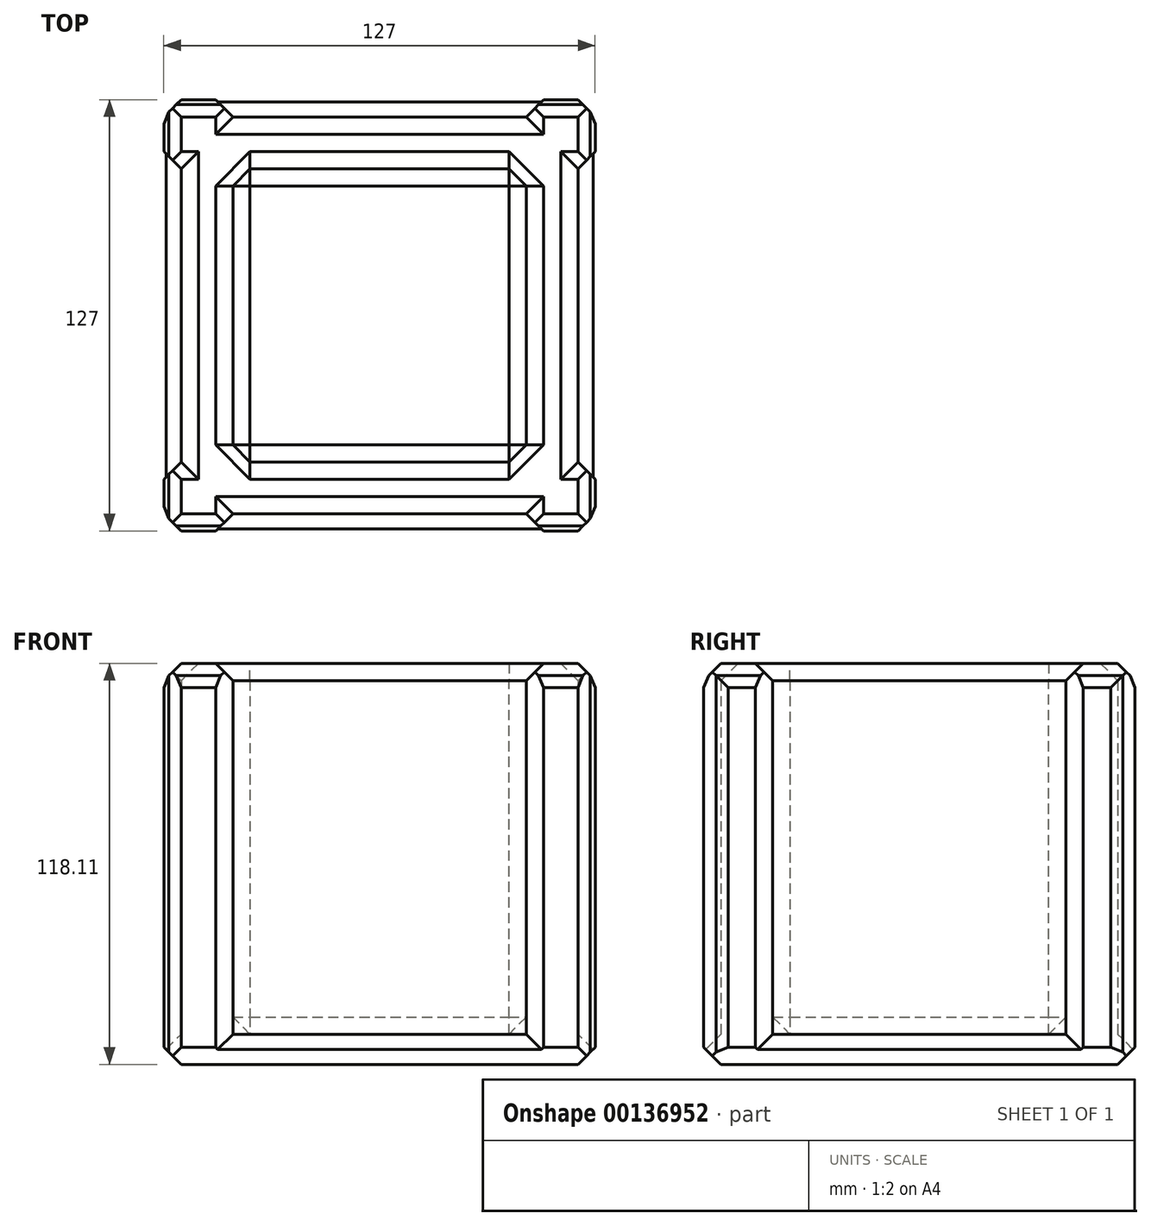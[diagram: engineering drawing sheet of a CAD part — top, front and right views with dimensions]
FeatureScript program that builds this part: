
annotation { "Feature Type Name" : "Feature", "Feature Type Description" : "" }
export const myFeature = defineFeature(function(context is Context, id is Id, definition is map)
    precondition{}
    {
        {
            var Q0;
            Q0=qCreatedBy(makeId("Top.planeOp"),FACE);
            var sketch = newSketch(context, id + "F0", { "sketchPlane" : qUnion([Q0])});
            skLineSegment(sketch, "E0.bottom", {"start": v(-59.79, 56.04) * mm, "end": v(67.21, 56.04) * mm});
            skLineSegment(sketch, "E0.top", {"start": v(-59.79, -70.96) * mm, "end": v(67.21, -70.96) * mm});
            skLineSegment(sketch, "E0.left", {"start": v(-59.79, 56.04) * mm, "end": v(-59.79, -70.96) * mm});
            skLineSegment(sketch, "E0.right", {"start": v(67.21, 56.04) * mm, "end": v(67.21, -70.96) * mm});
            skSolve(sketch);
        }
        {
            var Q0;
            Q0=makeQuery(id+"F0.imprint","IMPRINT",FACE,{"disambiguationData":[TD([[makeQuery(id+"F0.imprint","IMPRINT",EDGE,{"derivedFrom":sQuery(id+"F0.wireOp",EDGE,"E0.bottom")}),-1.0]])]});
            extrude(context, id + "F1", {"entities" : qUnion([Q0]), "depth" : 8.9 * mm});
        }
        {
            var Q0;
            Q0=makeQuery(id+"F1.opExtrude","CAP_FACE",FACE,{"disambiguationData":[OSD([sQuery(id+"F0.wireOp",EDGE,"E0.bottom"),sQuery(id+"F0.wireOp",EDGE,"E0.top"),sQuery(id+"F0.wireOp",EDGE,"E0.left"),sQuery(id+"F0.wireOp",EDGE,"E0.right")])],"isStart":false});
            var sketch = newSketch(context, id + "F2", { "sketchPlane" : qUnion([Q0])});
            skLineSegment(sketch, "E1.bottom", {"start": v(-59.79, -70.96) * mm, "end": v(-39.47, -70.96) * mm});
            skLineSegment(sketch, "E1.top", {"start": v(-59.79, -50.64) * mm, "end": v(-39.47, -50.64) * mm});
            skLineSegment(sketch, "E1.left", {"start": v(-59.79, -70.96) * mm, "end": v(-59.79, -50.64) * mm});
            skLineSegment(sketch, "E1.right", {"start": v(-39.47, -70.96) * mm, "end": v(-39.47, -50.64) * mm});
            skLineSegment(sketch, "E2.bottom", {"start": v(-59.79, 56.04) * mm, "end": v(-39.47, 56.04) * mm});
            skLineSegment(sketch, "E2.top", {"start": v(-59.79, 35.72) * mm, "end": v(-39.47, 35.72) * mm});
            skLineSegment(sketch, "E2.left", {"start": v(-59.79, 56.04) * mm, "end": v(-59.79, 35.72) * mm});
            skLineSegment(sketch, "E2.right", {"start": v(-39.47, 56.04) * mm, "end": v(-39.47, 35.72) * mm});
            skLineSegment(sketch, "E3.bottom", {"start": v(67.21, 56.04) * mm, "end": v(46.9, 56.04) * mm});
            skLineSegment(sketch, "E3.top", {"start": v(67.21, 35.72) * mm, "end": v(46.9, 35.72) * mm});
            skLineSegment(sketch, "E3.left", {"start": v(67.21, 56.04) * mm, "end": v(67.21, 35.72) * mm});
            skLineSegment(sketch, "E3.right", {"start": v(46.9, 56.04) * mm, "end": v(46.9, 35.72) * mm});
            skLineSegment(sketch, "E4.bottom", {"start": v(67.21, -70.96) * mm, "end": v(46.9, -70.96) * mm});
            skLineSegment(sketch, "E4.top", {"start": v(67.21, -50.64) * mm, "end": v(46.9, -50.64) * mm});
            skLineSegment(sketch, "E4.left", {"start": v(67.21, -70.96) * mm, "end": v(67.21, -50.64) * mm});
            skLineSegment(sketch, "E4.right", {"start": v(46.9, -70.96) * mm, "end": v(46.9, -50.64) * mm});
            skLineSegment(sketch, "E5", {"start": v(-39.47, 45.88) * mm, "end": v(46.9, 45.88) * mm});
            skLineSegment(sketch, "E6", {"start": v(57.05, 35.72) * mm, "end": v(57.05, -50.64) * mm});
            skLineSegment(sketch, "E7", {"start": v(46.9, -60.8) * mm, "end": v(-39.47, -60.8) * mm});
            skLineSegment(sketch, "E8", {"start": v(-49.63, -50.64) * mm, "end": v(-49.63, 35.72) * mm});
            skLineSegment(sketch, "E9", {"start": v(-39.47, 35.72) * mm, "end": v(-39.47, -50.64) * mm});
            skLineSegment(sketch, "E10", {"start": v(-39.47, -50.64) * mm, "end": v(46.9, -50.64) * mm});
            skLineSegment(sketch, "E11", {"start": v(46.9, -50.64) * mm, "end": v(46.9, 35.72) * mm});
            skLineSegment(sketch, "E12", {"start": v(46.9, 35.72) * mm, "end": v(-39.47, 35.72) * mm});
            skSolve(sketch);
        }
        {
            var Q0;
            {var subQ5=sQuery(id+"F2.wireOp",EDGE,"E2.bottom");Q0=makeQuery(id+"F2.imprint","IMPRINT",FACE,{"disambiguationData":[TD([[makeQuery(id+"F2.imprint","IMPRINT",EDGE,{"derivedFrom":subQ5}),-1.0]])]});}
            var Q1;
            {var subQ2=sQuery(id+"F2.wireOp",EDGE,"E5");Q1=makeQuery(id+"F2.imprint","IMPRINT",FACE,{"disambiguationData":[TD([[makeQuery(id+"F2.imprint","IMPRINT",EDGE,{"derivedFrom":subQ2}),-1.0]])]});}
            var Q2;
            {var subQ6=sQuery(id+"F2.wireOp",EDGE,"E3.bottom");Q2=makeQuery(id+"F2.imprint","IMPRINT",FACE,{"disambiguationData":[TD([[makeQuery(id+"F2.imprint","IMPRINT",EDGE,{"derivedFrom":subQ6}),-1.0]])]});}
            var Q3;
            {var subQ2=sQuery(id+"F2.wireOp",EDGE,"E6");Q3=makeQuery(id+"F2.imprint","IMPRINT",FACE,{"disambiguationData":[TD([[makeQuery(id+"F2.imprint","IMPRINT",EDGE,{"derivedFrom":subQ2}),-1.0]])]});}
            var Q4;
            {var subQ2=sQuery(id+"F2.wireOp",EDGE,"E8");Q4=makeQuery(id+"F2.imprint","IMPRINT",FACE,{"disambiguationData":[TD([[makeQuery(id+"F2.imprint","IMPRINT",EDGE,{"derivedFrom":subQ2}),-1.0]])]});}
            var Q5;
            {var subQ5=sQuery(id+"F2.wireOp",EDGE,"E1.bottom");Q5=makeQuery(id+"F2.imprint","IMPRINT",FACE,{"disambiguationData":[TD([[makeQuery(id+"F2.imprint","IMPRINT",EDGE,{"derivedFrom":subQ5}),1.0]])]});}
            var Q6;
            {var subQ5=sQuery(id+"F2.wireOp",EDGE,"E4.bottom");Q6=makeQuery(id+"F2.imprint","IMPRINT",FACE,{"disambiguationData":[TD([[makeQuery(id+"F2.imprint","IMPRINT",EDGE,{"derivedFrom":subQ5}),1.0]])]});}
            var Q7;
            {var subQ2=sQuery(id+"F2.wireOp",EDGE,"E7");Q7=makeQuery(id+"F2.imprint","IMPRINT",FACE,{"disambiguationData":[TD([[makeQuery(id+"F2.imprint","IMPRINT",EDGE,{"derivedFrom":subQ2}),-1.0]])]});}
            extrude(context, id + "F3", {"entities" : qUnion([Q0, Q1, Q2, Q3, Q4, Q5, Q6, Q7]), "operationType" : NewBodyOperationType.ADD, "depth" : 101.6 * mm});
        }
        {
            var Q0;
            Q0=makeQuery(id+"F3.opExtrude","CAP_FACE",FACE,{"disambiguationData":[OSD([sQuery(id+"F2.wireOp",EDGE,"E1.bottom"),sQuery(id+"F2.wireOp",EDGE,"E1.top"),sQuery(id+"F2.wireOp",EDGE,"E1.left"),sQuery(id+"F2.wireOp",EDGE,"E1.right"),sQuery(id+"F2.wireOp",EDGE,"E2.bottom"),sQuery(id+"F2.wireOp",EDGE,"E2.top"),sQuery(id+"F2.wireOp",EDGE,"E2.left"),sQuery(id+"F2.wireOp",EDGE,"E2.right"),sQuery(id+"F2.wireOp",EDGE,"E3.bottom"),sQuery(id+"F2.wireOp",EDGE,"E3.top"),sQuery(id+"F2.wireOp",EDGE,"E3.left"),sQuery(id+"F2.wireOp",EDGE,"E3.right"),sQuery(id+"F2.wireOp",EDGE,"E4.bottom"),sQuery(id+"F2.wireOp",EDGE,"E4.top"),sQuery(id+"F2.wireOp",EDGE,"E4.left"),sQuery(id+"F2.wireOp",EDGE,"E4.right"),sQuery(id+"F2.wireOp",EDGE,"E5"),sQuery(id+"F2.wireOp",EDGE,"E6"),sQuery(id+"F2.wireOp",EDGE,"E7"),sQuery(id+"F2.wireOp",EDGE,"E8"),sQuery(id+"F2.wireOp",EDGE,"E9"),sQuery(id+"F2.wireOp",EDGE,"E10"),sQuery(id+"F2.wireOp",EDGE,"E11"),sQuery(id+"F2.wireOp",EDGE,"E12")])],"isStart":false});
            var sketch = newSketch(context, id + "F4", { "sketchPlane" : qUnion([Q0])});
            skLineSegment(sketch, "E13.0", {"start": v(52.05, 50.89) * mm, "end": v(52.05, 40.87) * mm});
            skLineSegment(sketch, "E13.1", {"start": v(62.06, 50.89) * mm, "end": v(52.05, 50.89) * mm});
            skLineSegment(sketch, "E13.2", {"start": v(62.06, -55.8) * mm, "end": v(52.05, -55.8) * mm});
            skLineSegment(sketch, "E13.3", {"start": v(62.06, -65.81) * mm, "end": v(62.06, -55.8) * mm});
            skLineSegment(sketch, "E13.4", {"start": v(-44.62, -65.81) * mm, "end": v(-44.62, -55.8) * mm});
            skLineSegment(sketch, "E13.5", {"start": v(62.06, 40.87) * mm, "end": v(62.06, 50.89) * mm});
            skLineSegment(sketch, "E13.6", {"start": v(-54.63, -65.81) * mm, "end": v(-44.62, -65.81) * mm});
            skLineSegment(sketch, "E13.7", {"start": v(-54.63, 50.89) * mm, "end": v(-54.63, 40.87) * mm});
            skLineSegment(sketch, "E13.8", {"start": v(-54.63, 40.87) * mm, "end": v(-44.62, 40.87) * mm});
            skLineSegment(sketch, "E13.9", {"start": v(52.05, -65.81) * mm, "end": v(62.06, -65.81) * mm});
            skLineSegment(sketch, "E13.10", {"start": v(51.9, -55.65) * mm, "end": v(51.9, 40.73) * mm});
            skLineSegment(sketch, "E13.11", {"start": v(-44.47, 40.73) * mm, "end": v(-44.47, -55.65) * mm});
            skLineSegment(sketch, "E13.12", {"start": v(51.9, 40.73) * mm, "end": v(-44.47, 40.73) * mm});
            skLineSegment(sketch, "E13.13", {"start": v(52.05, -55.8) * mm, "end": v(52.05, -65.81) * mm});
            skLineSegment(sketch, "E13.14", {"start": v(-44.47, -55.65) * mm, "end": v(51.9, -55.65) * mm});
            skLineSegment(sketch, "E13.15", {"start": v(-44.62, 40.87) * mm, "end": v(-44.62, 50.89) * mm});
            skLineSegment(sketch, "E13.16", {"start": v(-44.62, -55.8) * mm, "end": v(-54.63, -55.8) * mm});
            skLineSegment(sketch, "E13.17", {"start": v(52.05, 40.87) * mm, "end": v(62.06, 40.87) * mm});
            skLineSegment(sketch, "E13.18", {"start": v(-44.62, 50.89) * mm, "end": v(-54.63, 50.89) * mm});
            skLineSegment(sketch, "E13.19", {"start": v(-54.63, -55.8) * mm, "end": v(-54.63, -65.81) * mm});
            skSolve(sketch);
        }
        {
            var Q0;
            Q0=makeQuery(id+"F4.imprint","IMPRINT",FACE,{"disambiguationData":[TD([[makeQuery(id+"F4.imprint","IMPRINT",EDGE,{"derivedFrom":sQuery(id+"F4.wireOp",EDGE,"E13.10")}),1.0]])]});
            var Q1;
            Q1=makeQuery(id+"F4.imprint","IMPRINT",FACE,{"disambiguationData":[TD([[makeQuery(id+"F4.imprint","IMPRINT",EDGE,{"derivedFrom":sQuery(id+"F4.wireOp",EDGE,"E13.7")}),1.0]])]});
            var Q2;
            Q2=makeQuery(id+"F4.imprint","IMPRINT",FACE,{"disambiguationData":[TD([[makeQuery(id+"F4.imprint","IMPRINT",EDGE,{"derivedFrom":sQuery(id+"F4.wireOp",EDGE,"E13.0")}),1.0]])]});
            var Q3;
            Q3=makeQuery(id+"F4.imprint","IMPRINT",FACE,{"disambiguationData":[TD([[makeQuery(id+"F4.imprint","IMPRINT",EDGE,{"derivedFrom":sQuery(id+"F4.wireOp",EDGE,"E13.4")}),1.0]])]});
            var Q4;
            Q4=makeQuery(id+"F4.imprint","IMPRINT",FACE,{"disambiguationData":[TD([[makeQuery(id+"F4.imprint","IMPRINT",EDGE,{"derivedFrom":sQuery(id+"F4.wireOp",EDGE,"E13.2")}),1.0]])]});
            var Q5;
            Q5=makeQuery(id+"F4.imprint","IMPRINT",FACE,{"disambiguationData":[TD([[makeQuery(id+"F4.imprint","IMPRINT",EDGE,{"derivedFrom":sQuery(id+"F4.wireOp",EDGE,"E13.0")}),-1.0]])]});
            extrude(context, id + "F5", {"entities" : qUnion([Q0, Q1, Q2, Q3, Q4, Q5]), "operationType" : NewBodyOperationType.ADD, "depth" : 7.62 * mm});
        }
        {
            var Q0;
            {var subQ0=sQuery(id+"F0.wireOp",EDGE,"E0.bottom");Q0=makeQuery(id+"F3.boolean.opBoolean","SPLIT",FACE,{"disambiguationData":[TD([makeQuery(id+"F1.opExtrude","SWEPT_FACE",FACE,{"disambiguationData":[OSD([subQ0])]})])],"derivedFrom":makeQuery(id+"F1.opExtrude","CAP_FACE",FACE,{"disambiguationData":[OSD([subQ0,sQuery(id+"F0.wireOp",EDGE,"E0.top"),sQuery(id+"F0.wireOp",EDGE,"E0.left"),sQuery(id+"F0.wireOp",EDGE,"E0.right")])],"isStart":false})});}
            var sketch = newSketch(context, id + "F6", { "sketchPlane" : qUnion([Q0])});
            skLineSegment(sketch, "E14", {"start": v(-39.47, 50.96) * mm, "end": v(46.9, 50.96) * mm});
            skSolve(sketch);
        }
        {
            var Q0;
            {var subQ0=sQuery(id+"F0.wireOp",EDGE,"E0.right");Q0=makeQuery(id+"F3.boolean.opBoolean","SPLIT",FACE,{"disambiguationData":[TD([makeQuery(id+"F1.opExtrude","SWEPT_FACE",FACE,{"disambiguationData":[OSD([subQ0])]})])],"derivedFrom":makeQuery(id+"F1.opExtrude","CAP_FACE",FACE,{"disambiguationData":[OSD([sQuery(id+"F0.wireOp",EDGE,"E0.bottom"),sQuery(id+"F0.wireOp",EDGE,"E0.top"),sQuery(id+"F0.wireOp",EDGE,"E0.left"),subQ0])],"isStart":false})});}
            var sketch = newSketch(context, id + "F7", { "sketchPlane" : qUnion([Q0])});
            skLineSegment(sketch, "E15", {"start": v(62.13, -50.64) * mm, "end": v(62.13, 35.72) * mm});
            skSolve(sketch);
        }
        {
            var Q0;
            {var subQ0=sQuery(id+"F0.wireOp",EDGE,"E0.top");Q0=makeQuery(id+"F3.boolean.opBoolean","SPLIT",FACE,{"disambiguationData":[TD([makeQuery(id+"F1.opExtrude","SWEPT_FACE",FACE,{"disambiguationData":[OSD([subQ0])]})])],"derivedFrom":makeQuery(id+"F1.opExtrude","CAP_FACE",FACE,{"disambiguationData":[OSD([sQuery(id+"F0.wireOp",EDGE,"E0.bottom"),subQ0,sQuery(id+"F0.wireOp",EDGE,"E0.left"),sQuery(id+"F0.wireOp",EDGE,"E0.right")])],"isStart":false})});}
            var sketch = newSketch(context, id + "F8", { "sketchPlane" : qUnion([Q0])});
            skLineSegment(sketch, "E16", {"start": v(46.9, -65.88) * mm, "end": v(-39.47, -65.88) * mm});
            skSolve(sketch);
        }
        {
            var Q0;
            {var subQ0=sQuery(id+"F0.wireOp",EDGE,"E0.left");Q0=makeQuery(id+"F3.boolean.opBoolean","SPLIT",FACE,{"disambiguationData":[TD([makeQuery(id+"F1.opExtrude","SWEPT_FACE",FACE,{"disambiguationData":[OSD([subQ0])]})])],"derivedFrom":makeQuery(id+"F1.opExtrude","CAP_FACE",FACE,{"disambiguationData":[OSD([sQuery(id+"F0.wireOp",EDGE,"E0.bottom"),sQuery(id+"F0.wireOp",EDGE,"E0.top"),subQ0,sQuery(id+"F0.wireOp",EDGE,"E0.right")])],"isStart":false})});}
            var sketch = newSketch(context, id + "F9", { "sketchPlane" : qUnion([Q0])});
            skLineSegment(sketch, "E17", {"start": v(-54.7, -50.64) * mm, "end": v(-54.7, 35.72) * mm});
            skSolve(sketch);
        }
        {
            var Q0;
            {var subQ0=sQuery(id+"F6.wireOp",EDGE,"E14");Q0=makeQuery(id+"F6.imprint","IMPRINT",FACE,{"disambiguationData":[TD([[makeQuery(id+"F6.imprint","IMPRINT",EDGE,{"derivedFrom":subQ0}),-1.0]])]});}
            var Q1;
            {var subQ0=sQuery(id+"F9.wireOp",EDGE,"E17");Q1=makeQuery(id+"F9.imprint","IMPRINT",FACE,{"disambiguationData":[TD([[makeQuery(id+"F9.imprint","IMPRINT",EDGE,{"derivedFrom":subQ0}),-1.0]])]});}
            var Q2;
            {var subQ0=sQuery(id+"F7.wireOp",EDGE,"E15");Q2=makeQuery(id+"F7.imprint","IMPRINT",FACE,{"disambiguationData":[TD([[makeQuery(id+"F7.imprint","IMPRINT",EDGE,{"derivedFrom":subQ0}),1.0]])]});}
            var Q3;
            {var subQ0=sQuery(id+"F8.wireOp",EDGE,"E16");Q3=makeQuery(id+"F8.imprint","IMPRINT",FACE,{"disambiguationData":[TD([[makeQuery(id+"F8.imprint","IMPRINT",EDGE,{"derivedFrom":subQ0}),-1.0]])]});}
            extrude(context, id + "F10", {"entities" : qUnion([Q0, Q1, Q2, Q3]), "operationType" : NewBodyOperationType.ADD, "depth" : 109.22 * mm});
        }
        {
            var Q0;
            {var subQ0=sQuery(id+"F2.wireOp",EDGE,"E8");var subQ1=sQuery(id+"F2.wireOp",EDGE,"E2.top");var subQ2=sQuery(id+"F2.wireOp",EDGE,"E1.top");var subQ3=sQuery(id+"F2.wireOp",EDGE,"E7");var subQ4=sQuery(id+"F2.wireOp",EDGE,"E4.right");var subQ5=sQuery(id+"F2.wireOp",EDGE,"E1.right");var subQ6=sQuery(id+"F2.wireOp",EDGE,"E6");var subQ7=sQuery(id+"F2.wireOp",EDGE,"E4.top");var subQ8=sQuery(id+"F2.wireOp",EDGE,"E3.top");var subQ9=sQuery(id+"F2.wireOp",EDGE,"E5");var subQ10=sQuery(id+"F2.wireOp",EDGE,"E3.right");var subQ11=sQuery(id+"F2.wireOp",EDGE,"E2.right");Q0=makeQuery(id+"F10.boolean.opBoolean","MERGE",FACE,{"derivedFrom":[makeQuery(id+"F5.opExtrude","CAP_FACE",FACE,{"disambiguationData":[OSD([sQuery(id+"F2.wireOp",EDGE,"E1.bottom"),subQ2,sQuery(id+"F2.wireOp",EDGE,"E1.left"),subQ5,sQuery(id+"F2.wireOp",EDGE,"E2.bottom"),subQ1,sQuery(id+"F2.wireOp",EDGE,"E2.left"),subQ11,sQuery(id+"F2.wireOp",EDGE,"E3.bottom"),subQ8,sQuery(id+"F2.wireOp",EDGE,"E3.left"),subQ10,sQuery(id+"F2.wireOp",EDGE,"E4.bottom"),subQ7,sQuery(id+"F2.wireOp",EDGE,"E4.left"),subQ4,subQ9,subQ6,subQ3,subQ0,sQuery(id+"F2.wireOp",EDGE,"E9"),sQuery(id+"F2.wireOp",EDGE,"E10"),sQuery(id+"F2.wireOp",EDGE,"E11"),sQuery(id+"F2.wireOp",EDGE,"E12")])],"isStart":false}),makeQuery(id+"F10.opExtrude","CAP_FACE",FACE,{"disambiguationData":[OSD([subQ11,subQ10,subQ9,sQuery(id+"F6.wireOp",EDGE,"E14")])],"isStart":false}),makeQuery(id+"F10.opExtrude","CAP_FACE",FACE,{"disambiguationData":[OSD([subQ8,subQ7,subQ6,sQuery(id+"F7.wireOp",EDGE,"E15")])],"isStart":false}),makeQuery(id+"F10.opExtrude","CAP_FACE",FACE,{"disambiguationData":[OSD([subQ5,subQ4,subQ3,sQuery(id+"F8.wireOp",EDGE,"E16")])],"isStart":false}),makeQuery(id+"F10.opExtrude","CAP_FACE",FACE,{"disambiguationData":[OSD([subQ2,subQ1,subQ0,sQuery(id+"F9.wireOp",EDGE,"E17")])],"isStart":false})]});}
            var Q1;
            {var subQ0=sQuery(id+"F2.wireOp",EDGE,"E9");Q1=makeQuery(id+"F5.boolean.opBoolean","MERGE",FACE,{"derivedFrom":[makeQuery(id+"F3.opExtrude","SWEPT_FACE",FACE,{"disambiguationData":[OSD([subQ0])]}),makeQuery(id+"F5.opExtrude","SWEPT_FACE",FACE,{"disambiguationData":[OSD([subQ0])]})]});}
            var Q2;
            {var subQ0=sQuery(id+"F2.wireOp",EDGE,"E12");Q2=makeQuery(id+"F5.boolean.opBoolean","MERGE",FACE,{"derivedFrom":[makeQuery(id+"F3.opExtrude","SWEPT_FACE",FACE,{"disambiguationData":[OSD([subQ0])]}),makeQuery(id+"F5.opExtrude","SWEPT_FACE",FACE,{"disambiguationData":[OSD([subQ0])]})]});}
            var Q3;
            {var subQ0=sQuery(id+"F2.wireOp",EDGE,"E11");Q3=makeQuery(id+"F5.boolean.opBoolean","MERGE",FACE,{"derivedFrom":[makeQuery(id+"F3.opExtrude","SWEPT_FACE",FACE,{"disambiguationData":[OSD([subQ0])]}),makeQuery(id+"F5.opExtrude","SWEPT_FACE",FACE,{"disambiguationData":[OSD([subQ0])]})]});}
            var Q4;
            {var subQ0=sQuery(id+"F2.wireOp",EDGE,"E10");Q4=makeQuery(id+"F5.boolean.opBoolean","MERGE",FACE,{"derivedFrom":[makeQuery(id+"F3.opExtrude","SWEPT_FACE",FACE,{"disambiguationData":[OSD([subQ0])]}),makeQuery(id+"F5.opExtrude","SWEPT_FACE",FACE,{"disambiguationData":[OSD([subQ0])]})]});}
            chamfer(context, id + "F11", {"entities" : qUnion([Q0, Q1, Q2, Q3, Q4]), "width" : 5.08 * mm, "tangentPropagation" : true});
        }
        {
            var Q0;
            {var subQ0=sQuery(id+"F2.wireOp",EDGE,"E3.bottom");var subQ1=sQuery(id+"F2.wireOp",EDGE,"E2.bottom");Q0=makeQuery(id+"F5.boolean.opBoolean","MERGE",FACE,{"derivedFrom":[makeQuery(id+"F3.boolean.opBoolean","MERGE",FACE,{"derivedFrom":[makeQuery(id+"F1.opExtrude","SWEPT_FACE",FACE,{"disambiguationData":[OSD([sQuery(id+"F0.wireOp",EDGE,"E0.bottom")])]}),makeQuery(id+"F3.opExtrude","SWEPT_FACE",FACE,{"disambiguationData":[OSD([subQ1])]}),makeQuery(id+"F3.opExtrude","SWEPT_FACE",FACE,{"disambiguationData":[OSD([subQ0])]})]}),makeQuery(id+"F5.opExtrude","SWEPT_FACE",FACE,{"disambiguationData":[OSD([subQ1])]}),makeQuery(id+"F5.opExtrude","SWEPT_FACE",FACE,{"disambiguationData":[OSD([subQ0])]})]});}
            var Q1;
            {var subQ0=sQuery(id+"F2.wireOp",EDGE,"E4.bottom");var subQ1=sQuery(id+"F2.wireOp",EDGE,"E1.bottom");Q1=makeQuery(id+"F5.boolean.opBoolean","MERGE",FACE,{"derivedFrom":[makeQuery(id+"F3.boolean.opBoolean","MERGE",FACE,{"derivedFrom":[makeQuery(id+"F1.opExtrude","SWEPT_FACE",FACE,{"disambiguationData":[OSD([sQuery(id+"F0.wireOp",EDGE,"E0.top")])]}),makeQuery(id+"F3.opExtrude","SWEPT_FACE",FACE,{"disambiguationData":[OSD([subQ1])]}),makeQuery(id+"F3.opExtrude","SWEPT_FACE",FACE,{"disambiguationData":[OSD([subQ0])]})]}),makeQuery(id+"F5.opExtrude","SWEPT_FACE",FACE,{"disambiguationData":[OSD([subQ1])]}),makeQuery(id+"F5.opExtrude","SWEPT_FACE",FACE,{"disambiguationData":[OSD([subQ0])]})]});}
            chamfer(context, id + "F12", {"entities" : qUnion([Q0, Q1]), "width" : 5.08 * mm, "tangentPropagation" : true});
        }
        {
            var Q0;
            {var subQ0=sQuery(id+"F2.wireOp",EDGE,"E2.left");var subQ1=sQuery(id+"F2.wireOp",EDGE,"E1.left");Q0=makeQuery(id+"F5.boolean.opBoolean","MERGE",FACE,{"derivedFrom":[makeQuery(id+"F3.boolean.opBoolean","MERGE",FACE,{"derivedFrom":[makeQuery(id+"F1.opExtrude","SWEPT_FACE",FACE,{"disambiguationData":[OSD([sQuery(id+"F0.wireOp",EDGE,"E0.left")])]}),makeQuery(id+"F3.opExtrude","SWEPT_FACE",FACE,{"disambiguationData":[OSD([subQ1])]}),makeQuery(id+"F3.opExtrude","SWEPT_FACE",FACE,{"disambiguationData":[OSD([subQ0])]})]}),makeQuery(id+"F5.opExtrude","SWEPT_FACE",FACE,{"disambiguationData":[OSD([subQ1])]}),makeQuery(id+"F5.opExtrude","SWEPT_FACE",FACE,{"disambiguationData":[OSD([subQ0])]})]});}
            var Q1;
            {var subQ0=sQuery(id+"F2.wireOp",EDGE,"E4.left");var subQ1=sQuery(id+"F2.wireOp",EDGE,"E3.left");Q1=makeQuery(id+"F5.boolean.opBoolean","MERGE",FACE,{"derivedFrom":[makeQuery(id+"F3.boolean.opBoolean","MERGE",FACE,{"derivedFrom":[makeQuery(id+"F1.opExtrude","SWEPT_FACE",FACE,{"disambiguationData":[OSD([sQuery(id+"F0.wireOp",EDGE,"E0.right")])]}),makeQuery(id+"F3.opExtrude","SWEPT_FACE",FACE,{"disambiguationData":[OSD([subQ1])]}),makeQuery(id+"F3.opExtrude","SWEPT_FACE",FACE,{"disambiguationData":[OSD([subQ0])]})]}),makeQuery(id+"F5.opExtrude","SWEPT_FACE",FACE,{"disambiguationData":[OSD([subQ1])]}),makeQuery(id+"F5.opExtrude","SWEPT_FACE",FACE,{"disambiguationData":[OSD([subQ0])]})]});}
            chamfer(context, id + "F13", {"entities" : qUnion([Q0, Q1]), "width" : 5.08 * mm, "tangentPropagation" : true});
        }
    });
